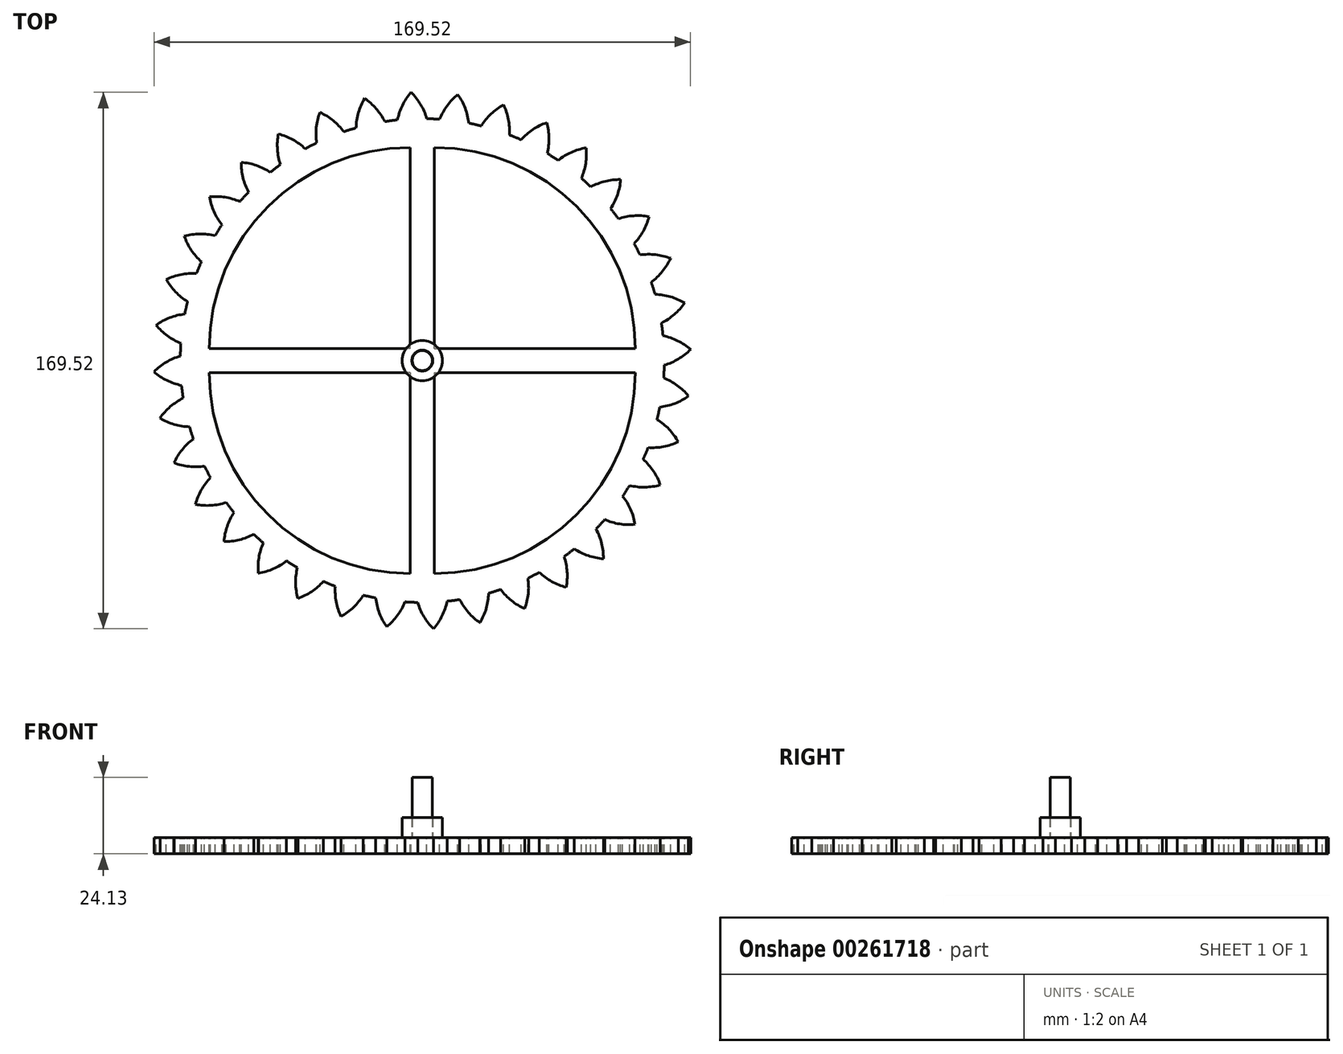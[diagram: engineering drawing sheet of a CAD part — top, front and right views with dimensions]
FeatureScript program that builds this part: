
annotation { "Feature Type Name" : "Feature", "Feature Type Description" : "" }
export const myFeature = defineFeature(function(context is Context, id is Id, definition is map)
    precondition{}
    {
        {
            var Q0;
            Q0=qCreatedBy(makeId("Top.planeOp"),FACE);
            var sketch = newSketch(context, id + "F0", { "sketchPlane" : qUnion([Q0])});
            skCircle(sketch, "E0", {"center": v(0, 0) * mm, "radius": 76.45 * mm});
            skSolve(sketch);
        }
        {
            var Q0;
            Q0=qSketchRegion(id+"F0",true);
            extrude(context, id + "F1", {"entities" : qUnion([Q0]), "depth" : 5.08 * mm});
        }
        {
            var Q0;
            Q0=makeQuery(id+"F1.opExtrude","CAP_FACE",FACE,{"disambiguationData":[OSD([sQuery(id+"F0.wireOp",EDGE,"E0")])],"isStart":false});
            var sketch = newSketch(context, id + "F2", { "sketchPlane" : qUnion([Q0])});
            skCircle(sketch, "E1", {"center": v(0, 0) * mm, "radius": 84.84 * mm, "construction": true});
            skCircle(sketch, "E2", {"center": v(0, 0) * mm, "radius": 80.01 * mm, "construction": true});
            skCircle(sketch, "E3", {"center": v(0, 0) * mm, "radius": 73.66 * mm, "construction": true});
            skLineSegment(sketch, "E4", {"start": v(0, 0) * mm, "end": v(0, 109.18) * mm, "construction": true});
            skLineSegment(sketch, "E5", {"start": v(0, 0) * mm, "end": v(-4.48, 106.79) * mm, "construction": true});
            skLineSegment(sketch, "E6", {"start": v(0, 80.01) * mm, "end": v(-65.71, 80.01) * mm, "construction": true});
            skLineSegment(sketch, "E7", {"start": v(0, 80.01) * mm, "end": v(-58.85, 53.8) * mm, "construction": true});
            skCircle(sketch, "E8", {"center": v(0, 80.01) * mm, "radius": 19.05 * mm, "construction": true});
            skCircle(sketch, "E9", {"center": v(0, 0) * mm, "radius": 73.1 * mm, "construction": true});
            skCircle(sketch, "E10", {"center": v(-16.85, 71.12) * mm, "radius": 19.05 * mm, "construction": true});
            skArc(sketch, "E11", {"start": v(2.03, 73.63) * mm, "mid": v(0.18, 79.67) * mm, "end": v(-3.55, 84.76) * mm});
            skArc(sketch, "E12.MirrorCS", {"start": v(-8.19, 73.2) * mm, "mid": v(-6.84, 79.37) * mm, "end": v(-3.56, 84.76) * mm});
            skLineSegment(sketch, "E13", {"start": v(-3.56, 84.76) * mm, "end": v(-3.55, 84.76) * mm});
            skLineSegment(sketch, "E14", {"start": v(-8.19, 73.2) * mm, "end": v(2.03, 73.63) * mm});
            skSolve(sketch);
        }
        {
            var Q0;
            Q0=qSketchRegion(id+"F2",true);
            var Q1;
            Q1=makeQuery(id+"F1.opExtrude","CAP_FACE",FACE,{"disambiguationData":[OSD([sQuery(id+"F0.wireOp",EDGE,"E0")])],"isStart":true});
            extrude(context, id + "F3", {"entities" : qUnion([Q0]), "endBound" : BoundingType.UP_TO_SURFACE, "oppositeDirection" : true, "endBoundEntityFace" : qUnion([Q1]), "depth" : 25.4 * mm});
        }
        {
            var Q0;
            Q0=makeQuery(id+"F3.opExtrude","SWEPT_BODY",BODY,{"disambiguationData":[OSD([sQuery(id+"F2.wireOp",EDGE,"E11"),sQuery(id+"F2.wireOp",EDGE,"E12.MirrorCS"),sQuery(id+"F2.wireOp",EDGE,"E13"),sQuery(id+"F2.wireOp",EDGE,"E14")])]});
            var Q1;
            Q1=makeQuery(id+"F1.opExtrude","CAP_EDGE",EDGE,{"disambiguationData":[OSD([sQuery(id+"F0.wireOp",EDGE,"E0")])],"isStart":false});
            circularPattern(context, id + "F4", {"operationType" : NewBodyOperationType.ADD, "entities" : qUnion([Q0]), "axis" : qUnion([Q1]), "angle" : 360 * degree, "instanceCount" : 36, "equalSpace" : true});
        }
        {
            var Q0;
            {var subQ0=makeQuery(id+"F3.opExtrude","CAP_FACE",FACE,{"disambiguationData":[OSD([sQuery(id+"F2.wireOp",EDGE,"E11"),sQuery(id+"F2.wireOp",EDGE,"E12.MirrorCS"),sQuery(id+"F2.wireOp",EDGE,"E13"),sQuery(id+"F2.wireOp",EDGE,"E14")])],"isStart":true});Q0=makeQuery(id+"F4.boolean.opBoolean","MERGE",FACE,{"derivedFrom":[makeQuery(id+"F1.opExtrude","CAP_FACE",FACE,{"disambiguationData":[OSD([sQuery(id+"F0.wireOp",EDGE,"E0")])],"isStart":false}),subQ0,makeQuery(id+"F4.opPattern","COPY",FACE,{"derivedFrom":subQ0,"instanceName":"1"}),makeQuery(id+"F4.opPattern","COPY",FACE,{"derivedFrom":subQ0,"instanceName":"2"}),makeQuery(id+"F4.opPattern","COPY",FACE,{"derivedFrom":subQ0,"instanceName":"3"}),makeQuery(id+"F4.opPattern","COPY",FACE,{"derivedFrom":subQ0,"instanceName":"4"}),makeQuery(id+"F4.opPattern","COPY",FACE,{"derivedFrom":subQ0,"instanceName":"5"}),makeQuery(id+"F4.opPattern","COPY",FACE,{"derivedFrom":subQ0,"instanceName":"6"}),makeQuery(id+"F4.opPattern","COPY",FACE,{"derivedFrom":subQ0,"instanceName":"7"}),makeQuery(id+"F4.opPattern","COPY",FACE,{"derivedFrom":subQ0,"instanceName":"8"}),makeQuery(id+"F4.opPattern","COPY",FACE,{"derivedFrom":subQ0,"instanceName":"9"}),makeQuery(id+"F4.opPattern","COPY",FACE,{"derivedFrom":subQ0,"instanceName":"10"}),makeQuery(id+"F4.opPattern","COPY",FACE,{"derivedFrom":subQ0,"instanceName":"11"}),makeQuery(id+"F4.opPattern","COPY",FACE,{"derivedFrom":subQ0,"instanceName":"12"}),makeQuery(id+"F4.opPattern","COPY",FACE,{"derivedFrom":subQ0,"instanceName":"13"}),makeQuery(id+"F4.opPattern","COPY",FACE,{"derivedFrom":subQ0,"instanceName":"14"}),makeQuery(id+"F4.opPattern","COPY",FACE,{"derivedFrom":subQ0,"instanceName":"15"}),makeQuery(id+"F4.opPattern","COPY",FACE,{"derivedFrom":subQ0,"instanceName":"16"}),makeQuery(id+"F4.opPattern","COPY",FACE,{"derivedFrom":subQ0,"instanceName":"17"}),makeQuery(id+"F4.opPattern","COPY",FACE,{"derivedFrom":subQ0,"instanceName":"18"}),makeQuery(id+"F4.opPattern","COPY",FACE,{"derivedFrom":subQ0,"instanceName":"19"}),makeQuery(id+"F4.opPattern","COPY",FACE,{"derivedFrom":subQ0,"instanceName":"20"}),makeQuery(id+"F4.opPattern","COPY",FACE,{"derivedFrom":subQ0,"instanceName":"21"}),makeQuery(id+"F4.opPattern","COPY",FACE,{"derivedFrom":subQ0,"instanceName":"22"}),makeQuery(id+"F4.opPattern","COPY",FACE,{"derivedFrom":subQ0,"instanceName":"23"}),makeQuery(id+"F4.opPattern","COPY",FACE,{"derivedFrom":subQ0,"instanceName":"24"}),makeQuery(id+"F4.opPattern","COPY",FACE,{"derivedFrom":subQ0,"instanceName":"25"}),makeQuery(id+"F4.opPattern","COPY",FACE,{"derivedFrom":subQ0,"instanceName":"26"}),makeQuery(id+"F4.opPattern","COPY",FACE,{"derivedFrom":subQ0,"instanceName":"27"}),makeQuery(id+"F4.opPattern","COPY",FACE,{"derivedFrom":subQ0,"instanceName":"28"}),makeQuery(id+"F4.opPattern","COPY",FACE,{"derivedFrom":subQ0,"instanceName":"29"}),makeQuery(id+"F4.opPattern","COPY",FACE,{"derivedFrom":subQ0,"instanceName":"30"}),makeQuery(id+"F4.opPattern","COPY",FACE,{"derivedFrom":subQ0,"instanceName":"31"}),makeQuery(id+"F4.opPattern","COPY",FACE,{"derivedFrom":subQ0,"instanceName":"32"}),makeQuery(id+"F4.opPattern","COPY",FACE,{"derivedFrom":subQ0,"instanceName":"33"}),makeQuery(id+"F4.opPattern","COPY",FACE,{"derivedFrom":subQ0,"instanceName":"34"}),makeQuery(id+"F4.opPattern","COPY",FACE,{"derivedFrom":subQ0,"instanceName":"35"})]});}
            var sketch = newSketch(context, id + "F5", { "sketchPlane" : qUnion([Q0])});
            skLineSegment(sketch, "E15", {"start": v(-3.81, 3.81) * mm, "end": v(-67.31, 3.8) * mm});
            skLineSegment(sketch, "E16", {"start": v(-3.81, 3.81) * mm, "end": v(-3.81, 67.31) * mm});
            skArc(sketch, "E17", {"start": v(-3.81, 67.31) * mm, "mid": v(-48.71, 48.71) * mm, "end": v(-67.31, 3.8) * mm});
            skArc(sketch, "E18.1.0", {"start": v(-67.31, -3.81) * mm, "mid": v(-48.71, -48.71) * mm, "end": v(-3.8, -67.3) * mm});
            skLineSegment(sketch, "E18.1.1", {"start": v(-3.81, -3.8) * mm, "end": v(-67.31, -3.81) * mm});
            skLineSegment(sketch, "E18.1.2", {"start": v(-3.81, -3.81) * mm, "end": v(-3.8, -67.31) * mm});
            skArc(sketch, "E18.2.0", {"start": v(3.81, -67.31) * mm, "mid": v(48.71, -48.71) * mm, "end": v(67.3, -3.81) * mm});
            skLineSegment(sketch, "E18.2.1", {"start": v(3.8, -3.81) * mm, "end": v(3.81, -67.31) * mm});
            skLineSegment(sketch, "E18.2.2", {"start": v(3.81, -3.81) * mm, "end": v(67.31, -3.8) * mm});
            skArc(sketch, "E18.3.0", {"start": v(67.3, 3.81) * mm, "mid": v(48.71, 48.71) * mm, "end": v(3.8, 67.31) * mm});
            skLineSegment(sketch, "E18.3.1", {"start": v(3.81, 3.8) * mm, "end": v(67.31, 3.81) * mm});
            skLineSegment(sketch, "E18.3.2", {"start": v(3.81, 3.81) * mm, "end": v(3.8, 67.31) * mm});
            skPoint(sketch, "E18.center", {"position": v(0, 0) * mm});
            skSolve(sketch);
        }
        {
            var Q0;
            Q0=qSketchRegion(id+"F5",true);
            extrude(context, id + "F6", {"entities" : qUnion([Q0]), "operationType" : NewBodyOperationType.REMOVE, "endBound" : BoundingType.THROUGH_ALL, "oppositeDirection" : true, "depth" : 25.4 * mm});
        }
        {
            var Q0;
            {var subQ0=makeQuery(id+"F3.opExtrude","CAP_FACE",FACE,{"disambiguationData":[OSD([sQuery(id+"F2.wireOp",EDGE,"E11"),sQuery(id+"F2.wireOp",EDGE,"E12.MirrorCS"),sQuery(id+"F2.wireOp",EDGE,"E13"),sQuery(id+"F2.wireOp",EDGE,"E14")])],"isStart":true});Q0=makeQuery(id+"F4.boolean.opBoolean","MERGE",FACE,{"derivedFrom":[makeQuery(id+"F1.opExtrude","CAP_FACE",FACE,{"disambiguationData":[OSD([sQuery(id+"F0.wireOp",EDGE,"E0")])],"isStart":false}),subQ0,makeQuery(id+"F4.opPattern","COPY",FACE,{"derivedFrom":subQ0,"instanceName":"1"}),makeQuery(id+"F4.opPattern","COPY",FACE,{"derivedFrom":subQ0,"instanceName":"2"}),makeQuery(id+"F4.opPattern","COPY",FACE,{"derivedFrom":subQ0,"instanceName":"3"}),makeQuery(id+"F4.opPattern","COPY",FACE,{"derivedFrom":subQ0,"instanceName":"4"}),makeQuery(id+"F4.opPattern","COPY",FACE,{"derivedFrom":subQ0,"instanceName":"5"}),makeQuery(id+"F4.opPattern","COPY",FACE,{"derivedFrom":subQ0,"instanceName":"6"}),makeQuery(id+"F4.opPattern","COPY",FACE,{"derivedFrom":subQ0,"instanceName":"7"}),makeQuery(id+"F4.opPattern","COPY",FACE,{"derivedFrom":subQ0,"instanceName":"8"}),makeQuery(id+"F4.opPattern","COPY",FACE,{"derivedFrom":subQ0,"instanceName":"9"}),makeQuery(id+"F4.opPattern","COPY",FACE,{"derivedFrom":subQ0,"instanceName":"10"}),makeQuery(id+"F4.opPattern","COPY",FACE,{"derivedFrom":subQ0,"instanceName":"11"}),makeQuery(id+"F4.opPattern","COPY",FACE,{"derivedFrom":subQ0,"instanceName":"12"}),makeQuery(id+"F4.opPattern","COPY",FACE,{"derivedFrom":subQ0,"instanceName":"13"}),makeQuery(id+"F4.opPattern","COPY",FACE,{"derivedFrom":subQ0,"instanceName":"14"}),makeQuery(id+"F4.opPattern","COPY",FACE,{"derivedFrom":subQ0,"instanceName":"15"}),makeQuery(id+"F4.opPattern","COPY",FACE,{"derivedFrom":subQ0,"instanceName":"16"}),makeQuery(id+"F4.opPattern","COPY",FACE,{"derivedFrom":subQ0,"instanceName":"17"}),makeQuery(id+"F4.opPattern","COPY",FACE,{"derivedFrom":subQ0,"instanceName":"18"}),makeQuery(id+"F4.opPattern","COPY",FACE,{"derivedFrom":subQ0,"instanceName":"19"}),makeQuery(id+"F4.opPattern","COPY",FACE,{"derivedFrom":subQ0,"instanceName":"20"}),makeQuery(id+"F4.opPattern","COPY",FACE,{"derivedFrom":subQ0,"instanceName":"21"}),makeQuery(id+"F4.opPattern","COPY",FACE,{"derivedFrom":subQ0,"instanceName":"22"}),makeQuery(id+"F4.opPattern","COPY",FACE,{"derivedFrom":subQ0,"instanceName":"23"}),makeQuery(id+"F4.opPattern","COPY",FACE,{"derivedFrom":subQ0,"instanceName":"24"}),makeQuery(id+"F4.opPattern","COPY",FACE,{"derivedFrom":subQ0,"instanceName":"25"}),makeQuery(id+"F4.opPattern","COPY",FACE,{"derivedFrom":subQ0,"instanceName":"26"}),makeQuery(id+"F4.opPattern","COPY",FACE,{"derivedFrom":subQ0,"instanceName":"27"}),makeQuery(id+"F4.opPattern","COPY",FACE,{"derivedFrom":subQ0,"instanceName":"28"}),makeQuery(id+"F4.opPattern","COPY",FACE,{"derivedFrom":subQ0,"instanceName":"29"}),makeQuery(id+"F4.opPattern","COPY",FACE,{"derivedFrom":subQ0,"instanceName":"30"}),makeQuery(id+"F4.opPattern","COPY",FACE,{"derivedFrom":subQ0,"instanceName":"31"}),makeQuery(id+"F4.opPattern","COPY",FACE,{"derivedFrom":subQ0,"instanceName":"32"}),makeQuery(id+"F4.opPattern","COPY",FACE,{"derivedFrom":subQ0,"instanceName":"33"}),makeQuery(id+"F4.opPattern","COPY",FACE,{"derivedFrom":subQ0,"instanceName":"34"}),makeQuery(id+"F4.opPattern","COPY",FACE,{"derivedFrom":subQ0,"instanceName":"35"})]});}
            var sketch = newSketch(context, id + "F7", { "sketchPlane" : qUnion([Q0])});
            skCircle(sketch, "E19", {"center": v(0, 0) * mm, "radius": 3.18 * mm});
            skSolve(sketch);
        }
        {
            var Q0;
            Q0=qSketchRegion(id+"F7",true);
            extrude(context, id + "F8", {"entities" : qUnion([Q0]), "operationType" : NewBodyOperationType.ADD, "depth" : 19.05 * mm});
        }
        {
            var Q0;
            {var subQ0=makeQuery(id+"F3.opExtrude","CAP_FACE",FACE,{"disambiguationData":[OSD([sQuery(id+"F2.wireOp",EDGE,"E11"),sQuery(id+"F2.wireOp",EDGE,"E12.MirrorCS"),sQuery(id+"F2.wireOp",EDGE,"E13"),sQuery(id+"F2.wireOp",EDGE,"E14")])],"isStart":true});Q0=makeQuery(id+"F4.boolean.opBoolean","MERGE",FACE,{"derivedFrom":[makeQuery(id+"F1.opExtrude","CAP_FACE",FACE,{"disambiguationData":[OSD([sQuery(id+"F0.wireOp",EDGE,"E0")])],"isStart":false}),subQ0,makeQuery(id+"F4.opPattern","COPY",FACE,{"derivedFrom":subQ0,"instanceName":"1"}),makeQuery(id+"F4.opPattern","COPY",FACE,{"derivedFrom":subQ0,"instanceName":"2"}),makeQuery(id+"F4.opPattern","COPY",FACE,{"derivedFrom":subQ0,"instanceName":"3"}),makeQuery(id+"F4.opPattern","COPY",FACE,{"derivedFrom":subQ0,"instanceName":"4"}),makeQuery(id+"F4.opPattern","COPY",FACE,{"derivedFrom":subQ0,"instanceName":"5"}),makeQuery(id+"F4.opPattern","COPY",FACE,{"derivedFrom":subQ0,"instanceName":"6"}),makeQuery(id+"F4.opPattern","COPY",FACE,{"derivedFrom":subQ0,"instanceName":"7"}),makeQuery(id+"F4.opPattern","COPY",FACE,{"derivedFrom":subQ0,"instanceName":"8"}),makeQuery(id+"F4.opPattern","COPY",FACE,{"derivedFrom":subQ0,"instanceName":"9"}),makeQuery(id+"F4.opPattern","COPY",FACE,{"derivedFrom":subQ0,"instanceName":"10"}),makeQuery(id+"F4.opPattern","COPY",FACE,{"derivedFrom":subQ0,"instanceName":"11"}),makeQuery(id+"F4.opPattern","COPY",FACE,{"derivedFrom":subQ0,"instanceName":"12"}),makeQuery(id+"F4.opPattern","COPY",FACE,{"derivedFrom":subQ0,"instanceName":"13"}),makeQuery(id+"F4.opPattern","COPY",FACE,{"derivedFrom":subQ0,"instanceName":"14"}),makeQuery(id+"F4.opPattern","COPY",FACE,{"derivedFrom":subQ0,"instanceName":"15"}),makeQuery(id+"F4.opPattern","COPY",FACE,{"derivedFrom":subQ0,"instanceName":"16"}),makeQuery(id+"F4.opPattern","COPY",FACE,{"derivedFrom":subQ0,"instanceName":"17"}),makeQuery(id+"F4.opPattern","COPY",FACE,{"derivedFrom":subQ0,"instanceName":"18"}),makeQuery(id+"F4.opPattern","COPY",FACE,{"derivedFrom":subQ0,"instanceName":"19"}),makeQuery(id+"F4.opPattern","COPY",FACE,{"derivedFrom":subQ0,"instanceName":"20"}),makeQuery(id+"F4.opPattern","COPY",FACE,{"derivedFrom":subQ0,"instanceName":"21"}),makeQuery(id+"F4.opPattern","COPY",FACE,{"derivedFrom":subQ0,"instanceName":"22"}),makeQuery(id+"F4.opPattern","COPY",FACE,{"derivedFrom":subQ0,"instanceName":"23"}),makeQuery(id+"F4.opPattern","COPY",FACE,{"derivedFrom":subQ0,"instanceName":"24"}),makeQuery(id+"F4.opPattern","COPY",FACE,{"derivedFrom":subQ0,"instanceName":"25"}),makeQuery(id+"F4.opPattern","COPY",FACE,{"derivedFrom":subQ0,"instanceName":"26"}),makeQuery(id+"F4.opPattern","COPY",FACE,{"derivedFrom":subQ0,"instanceName":"27"}),makeQuery(id+"F4.opPattern","COPY",FACE,{"derivedFrom":subQ0,"instanceName":"28"}),makeQuery(id+"F4.opPattern","COPY",FACE,{"derivedFrom":subQ0,"instanceName":"29"}),makeQuery(id+"F4.opPattern","COPY",FACE,{"derivedFrom":subQ0,"instanceName":"30"}),makeQuery(id+"F4.opPattern","COPY",FACE,{"derivedFrom":subQ0,"instanceName":"31"}),makeQuery(id+"F4.opPattern","COPY",FACE,{"derivedFrom":subQ0,"instanceName":"32"}),makeQuery(id+"F4.opPattern","COPY",FACE,{"derivedFrom":subQ0,"instanceName":"33"}),makeQuery(id+"F4.opPattern","COPY",FACE,{"derivedFrom":subQ0,"instanceName":"34"}),makeQuery(id+"F4.opPattern","COPY",FACE,{"derivedFrom":subQ0,"instanceName":"35"})]});}
            var sketch = newSketch(context, id + "F9", { "sketchPlane" : qUnion([Q0])});
            skCircle(sketch, "E20", {"center": v(0, 0) * mm, "radius": 6.35 * mm});
            skCircle(sketch, "E21", {"center": v(0, 0) * mm, "radius": 3.3 * mm});
            skSolve(sketch);
        }
        {
            var Q0;
            Q0 = qSketchRegion(id + "F9", true);
            extrude(context, id + "F10", {"entities" : qUnion([Q0]), "depth" : 6.35 * mm});
        }
    });
